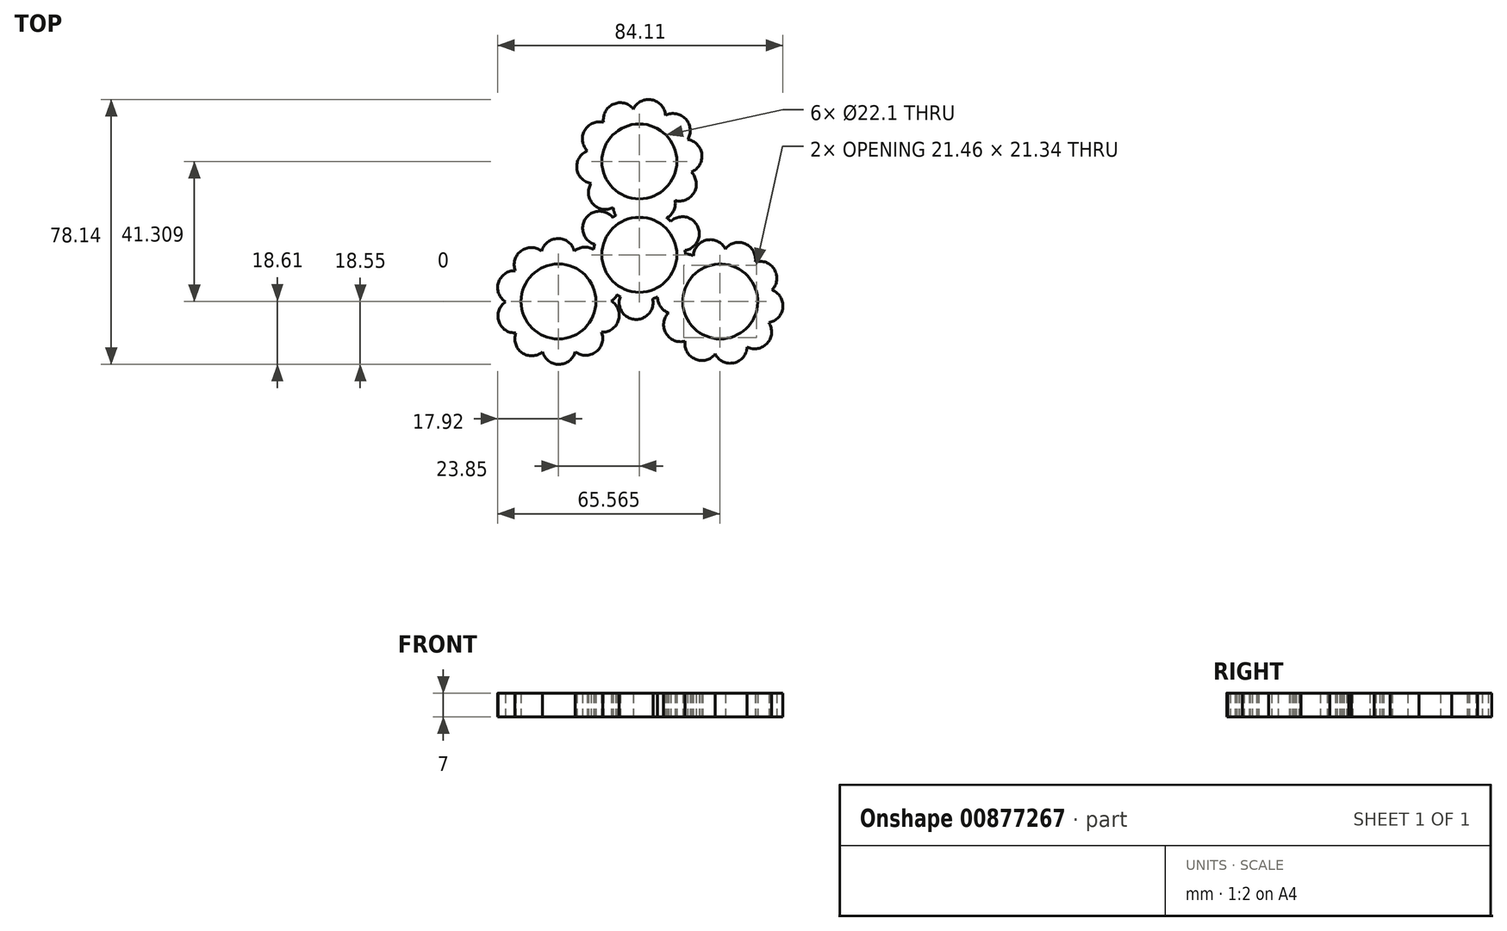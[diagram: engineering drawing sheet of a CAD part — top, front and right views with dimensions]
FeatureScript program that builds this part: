
annotation { "Feature Type Name" : "Feature", "Feature Type Description" : "" }
export const myFeature = defineFeature(function(context is Context, id is Id, definition is map)
    precondition{}
    {
        {
            var Q0;
            Q0=qCreatedBy(makeId("Top.planeOp"),FACE);
            var sketch = newSketch(context, id + "F0", { "sketchPlane" : qUnion([Q0])});
            skCircle(sketch, "E0", {"center": v(0, 0) * mm, "radius": 11.05 * mm});
            skCircle(sketch, "E1", {"center": v(0, 27.54) * mm, "radius": 11.05 * mm});
            skCircle(sketch, "E2.1.0", {"center": v(-23.85, -13.77) * mm, "radius": 11.05 * mm});
            skArc(sketch, "E2.2.0", {"start": v(18.63, -23.5) * mm, "mid": v(29.47, -4.26) * mm, "end": v(17.84, -23.04) * mm});
            skArc(sketch, "E3", {"start": v(-36.4, -23.06) * mm, "mid": v(-34.63, -28.87) * mm, "end": v(-28.55, -28.66) * mm});
            skArc(sketch, "E4.1.0", {"start": v(-28.55, -28.66) * mm, "mid": v(-23.7, -32.32) * mm, "end": v(-18.9, -28.58) * mm});
            skArc(sketch, "E4.2.0", {"start": v(-18.9, -28.58) * mm, "mid": v(-12.82, -28.68) * mm, "end": v(-11.14, -22.84) * mm});
            skArc(sketch, "E4.3.0", {"start": v(-11.14, -22.84) * mm, "mid": v(-6.16, -19.35) * mm, "end": v(-8.23, -13.64) * mm});
            skArc(sketch, "E4.5.0", {"start": v(-13.46, 1.58) * mm, "mid": v(-16.37, 2.24) * mm, "end": v(-19.15, 1.13) * mm});
            skArc(sketch, "E4.8.0", {"start": v(-36.56, -4.7) * mm, "mid": v(-41.54, -8.19) * mm, "end": v(-39.47, -13.9) * mm});
            skArc(sketch, "E4.9.0", {"start": v(-39.47, -13.9) * mm, "mid": v(-41.44, -19.65) * mm, "end": v(-36.4, -23.06) * mm});
            skArc(sketch, "E5", {"start": v(-7.86, 11.04) * mm, "mid": v(-15.88, 10.64) * mm, "end": v(-13.2, 3.08) * mm});
            skArc(sketch, "E6.1.0", {"start": v(-5.63, -12.33) * mm, "mid": v(-1.28, -19.07) * mm, "end": v(3.93, -12.97) * mm});
            skArc(sketch, "E6.2.0", {"start": v(13.49, 1.3) * mm, "mid": v(17.16, 8.43) * mm, "end": v(9.27, 9.89) * mm});
            skArc(sketch, "E7.trimOffspring", {"start": v(4.82, 12.66) * mm, "mid": v(4.82, 12.67) * mm, "end": v(4.83, 12.68) * mm});
            skArc(sketch, "E8.trimOffspring", {"start": v(-8.23, -13.64) * mm, "mid": v(-7.3, -12.84) * mm, "end": v(-6.6, -11.84) * mm});
            skPoint(sketch, "E9.center.orphan", {"position": v(0, 41.09) * mm});
            skLineSegment(sketch, "E10", {"start": v(17.84, -23.04) * mm, "end": v(18.63, -23.5) * mm});
            skArc(sketch, "E11.trimOffspring", {"start": v(-28.8, 1.04) * mm, "mid": v(-34.88, 1.14) * mm, "end": v(-36.56, -4.7) * mm});
            skArc(sketch, "E12.trimOffspring", {"start": v(-19.15, 1.13) * mm, "mid": v(-24, 4.78) * mm, "end": v(-28.8, 1.04) * mm});
            skArc(sketch, "E13.1.0", {"start": v(5.36, -12.44) * mm, "mid": v(6.24, -15.3) * mm, "end": v(8.6, -17.15) * mm});
            skArc(sketch, "E13.1.1", {"start": v(8.6, -17.15) * mm, "mid": v(7.86, -23.18) * mm, "end": v(13.5, -25.47) * mm});
            skArc(sketch, "E13.1.2", {"start": v(13.5, -25.47) * mm, "mid": v(16.45, -30.78) * mm, "end": v(22.35, -29.32) * mm});
            skArc(sketch, "E13.1.3", {"start": v(22.35, -29.32) * mm, "mid": v(27.86, -31.88) * mm, "end": v(31.77, -27.23) * mm});
            skArc(sketch, "E13.1.4", {"start": v(31.77, -27.23) * mm, "mid": v(37.74, -26.06) * mm, "end": v(38.17, -20) * mm});
            skArc(sketch, "E13.1.5", {"start": v(38.17, -20) * mm, "mid": v(42.31, -15.55) * mm, "end": v(39.1, -10.4) * mm});
            skArc(sketch, "E13.1.6", {"start": v(39.1, -10.4) * mm, "mid": v(39.84, -4.36) * mm, "end": v(34.2, -2.07) * mm});
            skArc(sketch, "E13.1.7", {"start": v(34.2, -2.07) * mm, "mid": v(31.25, 3.24) * mm, "end": v(25.35, 1.78) * mm});
            skArc(sketch, "E13.1.8", {"start": v(25.35, 1.78) * mm, "mid": v(19.84, 4.34) * mm, "end": v(15.93, -0.3) * mm});
            skArc(sketch, "E13.2.0", {"start": v(8.1, 10.87) * mm, "mid": v(10.13, 13.06) * mm, "end": v(10.55, 16.02) * mm});
            skArc(sketch, "E13.2.1", {"start": v(10.55, 16.02) * mm, "mid": v(16.14, 18.4) * mm, "end": v(15.3, 24.42) * mm});
            skArc(sketch, "E13.2.2", {"start": v(15.3, 24.42) * mm, "mid": v(18.43, 29.63) * mm, "end": v(14.21, 34.01) * mm});
            skArc(sketch, "E13.2.3", {"start": v(14.21, 34.01) * mm, "mid": v(13.68, 40.07) * mm, "end": v(7.7, 41.13) * mm});
            skArc(sketch, "E13.2.4", {"start": v(7.7, 41.13) * mm, "mid": v(3.7, 45.72) * mm, "end": v(-1.76, 43.06) * mm});
            skArc(sketch, "E13.2.5", {"start": v(-1.76, 43.06) * mm, "mid": v(-7.69, 44.42) * mm, "end": v(-10.55, 39.06) * mm});
            skArc(sketch, "E13.2.6", {"start": v(-10.55, 39.06) * mm, "mid": v(-16.14, 36.68) * mm, "end": v(-15.3, 30.66) * mm});
            skArc(sketch, "E13.2.7", {"start": v(-15.3, 30.66) * mm, "mid": v(-18.43, 25.44) * mm, "end": v(-14.21, 21.07) * mm});
            skArc(sketch, "E13.2.8", {"start": v(-14.21, 21.07) * mm, "mid": v(-13.68, 15.01) * mm, "end": v(-7.7, 13.95) * mm});
            skArc(sketch, "E14.1.1", {"start": v(15.93, -0.3) * mm, "mid": v(14.77, 0.1) * mm, "end": v(13.55, 0.2) * mm});
            skArc(sketch, "E14.2.1", {"start": v(-7.7, 13.95) * mm, "mid": v(-7.47, 12.74) * mm, "end": v(-6.96, 11.63) * mm});
            skArc(sketch, "E15", {"start": v(13.55, 0.2) * mm, "mid": v(13.53, 0.75) * mm, "end": v(13.49, 1.3) * mm});
            skPoint(sketch, "E16.orphan", {"position": v(9.53, -7.54) * mm});
            skPoint(sketch, "E17.orphan", {"position": v(11.04, -0.56) * mm});
            skArc(sketch, "E18.trimOffspring", {"start": v(3.93, -12.97) * mm, "mid": v(4.65, -12.73) * mm, "end": v(5.36, -12.44) * mm});
            skPoint(sketch, "E19.orphan", {"position": v(-6, -9.28) * mm});
            skPoint(sketch, "E20.orphan", {"position": v(-11.3, -4.48) * mm});
            skArc(sketch, "E21.trimOffspring", {"start": v(-6.6, -11.84) * mm, "mid": v(-6.11, -12.1) * mm, "end": v(-5.63, -12.33) * mm});
            skArc(sketch, "E22.trimOffspring", {"start": v(-13.2, 3.08) * mm, "mid": v(-13.35, 2.33) * mm, "end": v(-13.46, 1.58) * mm});
            skPoint(sketch, "E23.orphan", {"position": v(-6.8, 8.71) * mm});
            skPoint(sketch, "E24.orphan", {"position": v(-5.03, 9.84) * mm});
            skPoint(sketch, "E25.orphan", {"position": v(1.76, 12.02) * mm});
            skPoint(sketch, "E26.center.orphan", {"position": v(0, 8.71) * mm});
            skArc(sketch, "E27.trimOffspring", {"start": v(-6.96, 11.63) * mm, "mid": v(-7.41, 11.34) * mm, "end": v(-7.86, 11.04) * mm});
            skArc(sketch, "E28.trimOffspring", {"start": v(9.27, 9.89) * mm, "mid": v(8.7, 10.4) * mm, "end": v(8.1, 10.87) * mm});
            skSolve(sketch);
        }
        {
            var Q0;
            Q0=makeQuery(id+"F0.imprint","IMPRINT",FACE,{"disambiguationData":[TD([[makeQuery(id+"F0.imprint","IMPRINT",EDGE,{"derivedFrom":sQuery(id+"F0.wireOp",EDGE,"E2.1.0")}),-1.0]])]});
            var Q1;
            Q1=makeQuery(id+"F0.imprint","IMPRINT",FACE,{"disambiguationData":[TD([[makeQuery(id+"F0.imprint","IMPRINT",EDGE,{"derivedFrom":sQuery(id+"F0.wireOp",EDGE,"E1")}),-1.0]])]});
            var Q2;
            {var subQ0=sQuery(id+"F0.wireOp",EDGE,"E15");var subQ1=sQuery(id+"F0.wireOp",EDGE,"E5");var subQ2=makeQuery(id+"F0.imprint","INTERSECT",VERTEX,{"disambiguationData":[OD(0.0)],"derivedFrom":[subQ1,subQ0]});Q2=makeQuery(id+"F0.imprint","IMPRINT",FACE,{"disambiguationData":[TD([[makeQuery(id+"F0.imprint","IMPRINT",EDGE,{"disambiguationData":[TD([[subQ2,-1.0]])],"derivedFrom":subQ1}),1.0]])]});}
            var Q3;
            {var subQ0=sQuery(id+"F0.wireOp",EDGE,"E15");var subQ1=sQuery(id+"F0.wireOp",EDGE,"E6.2.0");var subQ2=makeQuery(id+"F0.imprint","INTERSECT",VERTEX,{"disambiguationData":[OD(0.0)],"derivedFrom":[subQ1,subQ0]});Q3=makeQuery(id+"F0.imprint","IMPRINT",FACE,{"disambiguationData":[TD([[makeQuery(id+"F0.imprint","IMPRINT",EDGE,{"disambiguationData":[TD([[subQ2,-1.0]])],"derivedFrom":subQ1}),1.0]])]});}
            var Q4;
            Q4=makeQuery(id+"F0.imprint","IMPRINT",FACE,{"disambiguationData":[TD([[makeQuery(id+"F0.imprint","IMPRINT",EDGE,{"derivedFrom":sQuery(id+"F0.wireOp",EDGE,"E2.2.0")}),-1.0]])]});
            var Q5;
            {var subQ0=sQuery(id+"F0.wireOp",EDGE,"E15");var subQ1=sQuery(id+"F0.wireOp",EDGE,"E6.1.0");var subQ2=makeQuery(id+"F0.imprint","INTERSECT",VERTEX,{"disambiguationData":[OD(0.0)],"derivedFrom":[subQ1,subQ0]});Q5=makeQuery(id+"F0.imprint","IMPRINT",FACE,{"disambiguationData":[TD([[makeQuery(id+"F0.imprint","IMPRINT",EDGE,{"disambiguationData":[TD([[subQ2,-1.0]])],"derivedFrom":subQ1}),1.0]])]});}
            var Q6;
            {var subQ0=sQuery(id+"F0.wireOp",EDGE,"E5");var subQ1=sQuery(id+"F0.wireOp",EDGE,"E0");var subQ2=makeQuery(id+"F0.imprint","INTERSECT",VERTEX,{"disambiguationData":[OD(0.0)],"derivedFrom":[subQ1,subQ0]});Q6=makeQuery(id+"F0.imprint","IMPRINT",FACE,{"disambiguationData":[TD([[makeQuery(id+"F0.imprint","IMPRINT",EDGE,{"disambiguationData":[TD([[subQ2,1.0]])],"derivedFrom":subQ1}),-1.0]])]});}
            var Q7;
            {var subQ0=sQuery(id+"F0.wireOp",EDGE,"E5");var subQ1=sQuery(id+"F0.wireOp",EDGE,"E0");var subQ2=makeQuery(id+"F0.imprint","INTERSECT",VERTEX,{"disambiguationData":[OD(0.0)],"derivedFrom":[subQ1,subQ0]});Q7=makeQuery(id+"F0.imprint","IMPRINT",FACE,{"disambiguationData":[TD([[makeQuery(id+"F0.imprint","IMPRINT",EDGE,{"disambiguationData":[TD([[subQ2,-1.0]])],"derivedFrom":subQ1}),-1.0]])]});}
            var Q8;
            {var subQ1=sQuery(id+"F0.wireOp",EDGE,"E0");var subQ5=sQuery(id+"F0.wireOp",EDGE,"E5");var subQ6=makeQuery(id+"F0.imprint","INTERSECT",VERTEX,{"disambiguationData":[OD(1.0)],"derivedFrom":[subQ1,subQ5]});Q8=makeQuery(id+"F0.imprint","IMPRINT",FACE,{"disambiguationData":[TD([[makeQuery(id+"F0.imprint","IMPRINT",EDGE,{"disambiguationData":[TD([[subQ6,-1.0]])],"derivedFrom":subQ1}),-1.0]])]});}
            var Q9;
            {var subQ0=sQuery(id+"F0.wireOp",EDGE,"E15");var subQ1=sQuery(id+"F0.wireOp",EDGE,"E4.5.0");var subQ2=makeQuery(id+"F0.imprint","INTERSECT",VERTEX,{"derivedFrom":[subQ1,subQ0]});Q9=makeQuery(id+"F0.imprint","IMPRINT",FACE,{"disambiguationData":[TD([[makeQuery(id+"F0.imprint","IMPRINT",EDGE,{"disambiguationData":[TD([[subQ2,1.0]])],"derivedFrom":subQ1}),1.0]])]});}
            var Q10;
            {var subQ1=sQuery(id+"F0.wireOp",EDGE,"E4.4.0");Q10=makeQuery(id+"F0.imprint","IMPRINT",FACE,{"disambiguationData":[TD([[makeQuery(id+"F0.imprint","IMPRINT",EDGE,{"derivedFrom":subQ1}),1.0]])]});}
            var Q11;
            {var subQ0=sQuery(id+"F0.wireOp",EDGE,"E4.4.0");Q11=makeQuery(id+"F0.imprint","IMPRINT",FACE,{"disambiguationData":[TD([[makeQuery(id+"F0.imprint","IMPRINT",EDGE,{"derivedFrom":subQ0}),-1.0]])]});}
            var Q12;
            {var subQ0=sQuery(id+"F0.wireOp",EDGE,"E15");var subQ1=sQuery(id+"F0.wireOp",EDGE,"71516dd6-7639-46da-99b2-bf78b63bb082.1.0");var subQ2=makeQuery(id+"F0.imprint","INTERSECT",VERTEX,{"disambiguationData":[OD(0.0)],"derivedFrom":[subQ1,subQ0]});Q12=makeQuery(id+"F0.imprint","IMPRINT",FACE,{"disambiguationData":[TD([[makeQuery(id+"F0.imprint","IMPRINT",EDGE,{"disambiguationData":[TD([[subQ2,-1.0]])],"derivedFrom":subQ1}),1.0]])]});}
            var Q13;
            {var subQ0=sQuery(id+"F0.wireOp",EDGE,"E6.1.0");var subQ1=sQuery(id+"F0.wireOp",EDGE,"E0");var subQ2=makeQuery(id+"F0.imprint","INTERSECT",VERTEX,{"disambiguationData":[OD(0.0)],"derivedFrom":[subQ1,subQ0]});Q13=makeQuery(id+"F0.imprint","IMPRINT",FACE,{"disambiguationData":[TD([[makeQuery(id+"F0.imprint","IMPRINT",EDGE,{"disambiguationData":[TD([[subQ2,1.0]])],"derivedFrom":subQ1}),-1.0]])]});}
            var Q14;
            {var subQ0=sQuery(id+"F0.wireOp",EDGE,"E8.trimOffspring");var subQ1=sQuery(id+"F0.wireOp",EDGE,"E0");var subQ2=makeQuery(id+"F0.imprint","INTERSECT",VERTEX,{"derivedFrom":[subQ1,subQ0]});Q14=makeQuery(id+"F0.imprint","IMPRINT",FACE,{"disambiguationData":[TD([[makeQuery(id+"F0.imprint","IMPRINT",EDGE,{"disambiguationData":[TD([[subQ2,1.0]])],"derivedFrom":subQ1}),-1.0]])]});}
            var Q15;
            {var subQ0=sQuery(id+"F0.wireOp",EDGE,"E6.1.0");var subQ1=sQuery(id+"F0.wireOp",EDGE,"E0");var subQ2=makeQuery(id+"F0.imprint","INTERSECT",VERTEX,{"disambiguationData":[OD(0.0)],"derivedFrom":[subQ1,subQ0]});Q15=makeQuery(id+"F0.imprint","IMPRINT",FACE,{"disambiguationData":[TD([[makeQuery(id+"F0.imprint","IMPRINT",EDGE,{"disambiguationData":[TD([[subQ2,-1.0]])],"derivedFrom":subQ1}),-1.0]])]});}
            var Q16;
            {var subQ5=sQuery(id+"F0.wireOp",EDGE,"E6.1.0");var subQ6=sQuery(id+"F0.wireOp",EDGE,"E0");var subQ7=makeQuery(id+"F0.imprint","INTERSECT",VERTEX,{"disambiguationData":[OD(1.0)],"derivedFrom":[subQ6,subQ5]});Q16=makeQuery(id+"F0.imprint","IMPRINT",FACE,{"disambiguationData":[TD([[makeQuery(id+"F0.imprint","IMPRINT",EDGE,{"disambiguationData":[TD([[subQ7,-1.0]])],"derivedFrom":subQ6}),-1.0]])]});}
            var Q17;
            {var subQ5=sQuery(id+"F0.wireOp",EDGE,"E14.1.0");Q17=makeQuery(id+"F0.imprint","IMPRINT",FACE,{"disambiguationData":[TD([[makeQuery(id+"F0.imprint","IMPRINT",EDGE,{"derivedFrom":subQ5}),1.0]])]});}
            extrude(context, id + "F1", {"entities" : qUnion([Q0, Q1, Q2, Q3, Q4, Q5, Q6, Q7, Q8, Q9, Q10, Q11, Q12, Q13, Q14, Q15, Q16, Q17]), "depth" : 7 * mm, "offsetDistance" : 25 * mm});
        }
        {
            var Q0;
            Q0 = qSketchRegion(id + "F0", true);
            var Q1;
            {var subQ0=sQuery(id+"F0.wireOp",EDGE,"E14.1.0");Q1=makeQuery(id+"F0.imprint","IMPRINT",FACE,{"disambiguationData":[TD([[makeQuery(id+"F0.imprint","IMPRINT",EDGE,{"derivedFrom":subQ0}),-1.0]])]});}
            var Q2;
            {var subQ0=sQuery(id+"F0.wireOp",EDGE,"E15");var subQ1=sQuery(id+"F0.wireOp",EDGE,"71516dd6-7639-46da-99b2-bf78b63bb082.2.0");var subQ2=makeQuery(id+"F0.imprint","INTERSECT",VERTEX,{"disambiguationData":[OD(0.0)],"derivedFrom":[subQ1,subQ0]});Q2=makeQuery(id+"F0.imprint","IMPRINT",FACE,{"disambiguationData":[TD([[makeQuery(id+"F0.imprint","IMPRINT",EDGE,{"disambiguationData":[TD([[subQ2,-1.0]])],"derivedFrom":subQ1}),1.0]])]});}
            var Q3;
            {var subQ5=sQuery(id+"F0.wireOp",EDGE,"E14.2.0");Q3=makeQuery(id+"F0.imprint","IMPRINT",FACE,{"disambiguationData":[TD([[makeQuery(id+"F0.imprint","IMPRINT",EDGE,{"derivedFrom":subQ5}),1.0]])]});}
            var Q4;
            {var subQ0=sQuery(id+"F0.wireOp",EDGE,"E14.2.0");Q4=makeQuery(id+"F0.imprint","IMPRINT",FACE,{"disambiguationData":[TD([[makeQuery(id+"F0.imprint","IMPRINT",EDGE,{"derivedFrom":subQ0}),-1.0]])]});}
            var Q5;
            {var subQ0=sQuery(id+"F0.wireOp",EDGE,"E15");var subQ1=sQuery(id+"F0.wireOp",EDGE,"E26");var subQ2=makeQuery(id+"F0.imprint","INTERSECT",VERTEX,{"disambiguationData":[OD(0.0)],"derivedFrom":[subQ1,subQ0]});Q5=makeQuery(id+"F0.imprint","IMPRINT",FACE,{"disambiguationData":[TD([[makeQuery(id+"F0.imprint","IMPRINT",EDGE,{"disambiguationData":[TD([[subQ2,-1.0]])],"derivedFrom":subQ1}),1.0]])]});}
            extrude(context, id + "F2", {"entities" : qUnion([Q0, Q1, Q2, Q3, Q4, Q5]), "depth" : 7 * mm, "offsetDistance" : 25 * mm});
        }
    });
